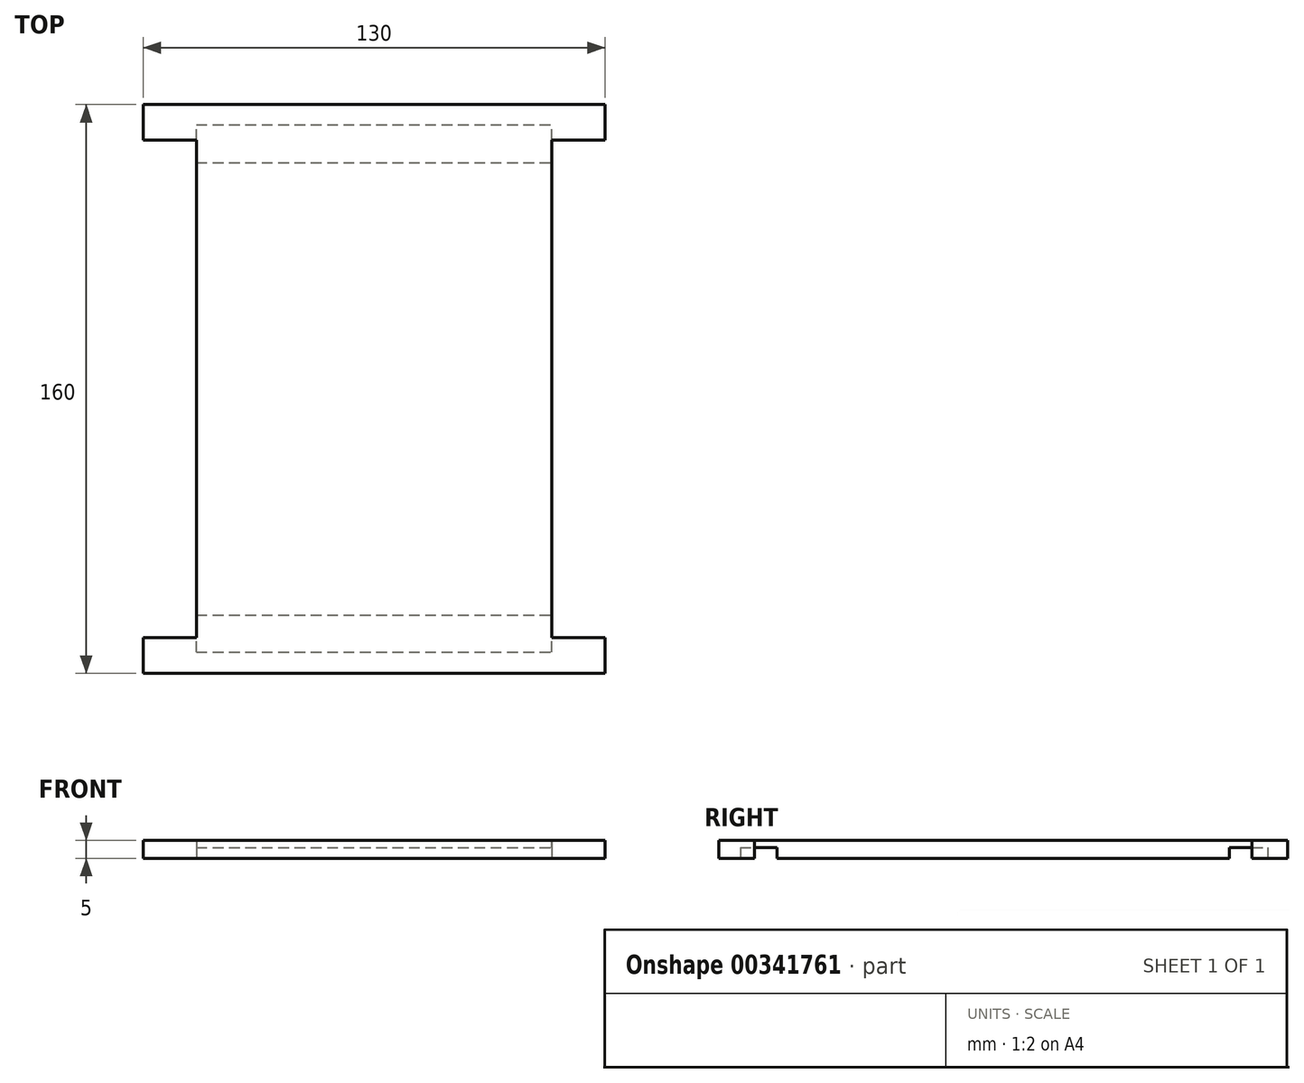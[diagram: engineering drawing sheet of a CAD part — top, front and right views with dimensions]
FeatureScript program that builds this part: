
annotation { "Feature Type Name" : "Feature", "Feature Type Description" : "" }
export const myFeature = defineFeature(function(context is Context, id is Id, definition is map)
    precondition{}
    {
        {
            var Q0;
            Q0=qCreatedBy(makeId("Top.planeOp"),FACE);
            var sketch = newSketch(context, id + "F0", { "sketchPlane" : qUnion([Q0])});
            skLineSegment(sketch, "E0", {"start": v(-65, 122.13) * mm, "end": v(-65, 132.13) * mm});
            skLineSegment(sketch, "E1", {"start": v(-65, 132.13) * mm, "end": v(0, 132.13) * mm});
            skLineSegment(sketch, "E2", {"start": v(-65, 122.13) * mm, "end": v(-50, 122.13) * mm});
            skLineSegment(sketch, "E3.MirrorCS", {"start": v(-65, -17.87) * mm, "end": v(-50, -17.87) * mm});
            skLineSegment(sketch, "E4.MirrorCS", {"start": v(-65, -17.87) * mm, "end": v(-65, -27.87) * mm});
            skLineSegment(sketch, "E5.MirrorCS", {"start": v(-65, -27.87) * mm, "end": v(0, -27.87) * mm});
            skLineSegment(sketch, "E6.MirrorCS", {"start": v(-50, -17.87) * mm, "end": v(-50, 122.13) * mm});
            skLineSegment(sketch, "E7.MirrorCS", {"start": v(0, 132.13) * mm, "end": v(65, 132.13) * mm});
            skLineSegment(sketch, "E8.MirrorCS", {"start": v(65, 122.13) * mm, "end": v(65, 132.13) * mm});
            skLineSegment(sketch, "E9.MirrorCS", {"start": v(65, 122.13) * mm, "end": v(50, 122.13) * mm});
            skLineSegment(sketch, "E10.MirrorCS", {"start": v(50, -21.84) * mm, "end": v(50, 122.13) * mm});
            skLineSegment(sketch, "E11.MirrorCS", {"start": v(65, -27.87) * mm, "end": v(0, -27.87) * mm});
            skLineSegment(sketch, "E12.MirrorCS", {"start": v(65, -17.87) * mm, "end": v(65, -27.87) * mm});
            skLineSegment(sketch, "E13.MirrorCS", {"start": v(65, -17.87) * mm, "end": v(50, -17.87) * mm});
            skLineSegment(sketch, "E14.bottom", {"start": v(-50, -11.52) * mm, "end": v(50, -11.52) * mm});
            skLineSegment(sketch, "E14.top", {"start": v(-50, -21.84) * mm, "end": v(50, -21.84) * mm});
            skLineSegment(sketch, "E14.left", {"start": v(-50, -11.52) * mm, "end": v(-50, -21.84) * mm});
            skLineSegment(sketch, "E14.right", {"start": v(50, -11.52) * mm, "end": v(50, -21.84) * mm});
            skLineSegment(sketch, "E15.bottom", {"start": v(-50, 126.48) * mm, "end": v(50, 126.48) * mm});
            skLineSegment(sketch, "E15.top", {"start": v(-50, 115.78) * mm, "end": v(50, 115.78) * mm});
            skLineSegment(sketch, "E15.left", {"start": v(-50, 126.48) * mm, "end": v(-50, 115.78) * mm});
            skLineSegment(sketch, "E15.right", {"start": v(50, 126.48) * mm, "end": v(50, 115.78) * mm});
            skSolve(sketch);
        }
        {
            var Q0;
            Q0 = qSketchRegion(id + "F0", true);
            extrude(context, id + "F1", {"entities" : qUnion([Q0]), "depth" : 5 * mm});
        }
        {
            var Q0;
            {var subQ3=sQuery(id+"F0.wireOp",EDGE,"E14.bottom");Q0=makeQuery(id+"F0.imprint","IMPRINT",FACE,{"disambiguationData":[TD([[makeQuery(id+"F0.imprint","IMPRINT",EDGE,{"derivedFrom":subQ3}),-1.0]])]});}
            extrude(context, id + "F2", {"entities" : qUnion([Q0]), "operationType" : NewBodyOperationType.REMOVE, "depth" : 3 * mm});
        }
        {
            var Q0;
            {var subQ3=sQuery(id+"F0.wireOp",EDGE,"E15.bottom");Q0=makeQuery(id+"F0.imprint","IMPRINT",FACE,{"disambiguationData":[TD([[makeQuery(id+"F0.imprint","IMPRINT",EDGE,{"derivedFrom":subQ3}),-1.0]])]});}
            extrude(context, id + "F3", {"entities" : qUnion([Q0]), "operationType" : NewBodyOperationType.REMOVE, "depth" : 3 * mm});
        }
    });
